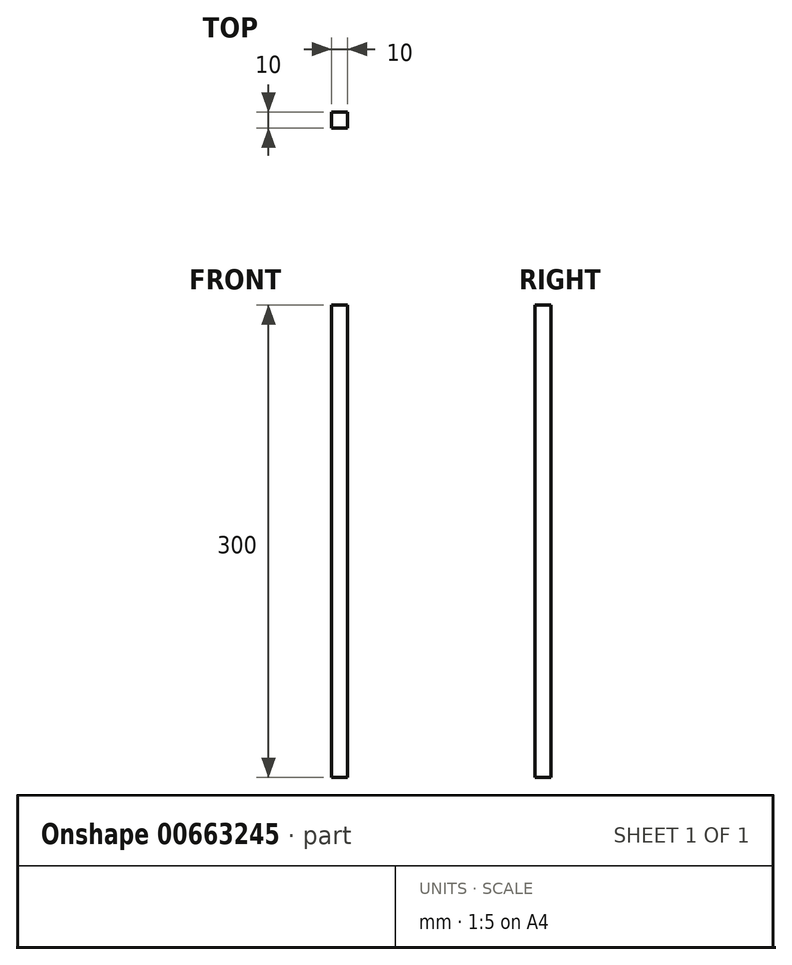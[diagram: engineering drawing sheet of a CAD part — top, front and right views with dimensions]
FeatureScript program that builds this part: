
annotation { "Feature Type Name" : "Feature", "Feature Type Description" : "" }
export const myFeature = defineFeature(function(context is Context, id is Id, definition is map)
    precondition{}
    {
        {
            var Q0;
            Q0=qCreatedBy(makeId("Top.planeOp"),FACE);
            var sketch = newSketch(context, id + "F0", { "sketchPlane" : qUnion([Q0])});
            skLineSegment(sketch, "E0.bottom", {"start": v(5, 5) * mm, "end": v(-5, 5) * mm});
            skLineSegment(sketch, "E0.top", {"start": v(5, -5) * mm, "end": v(-5, -5) * mm});
            skLineSegment(sketch, "E0.left", {"start": v(5, 5) * mm, "end": v(5, -5) * mm});
            skLineSegment(sketch, "E0.right", {"start": v(-5, 5) * mm, "end": v(-5, -5) * mm});
            skPoint(sketch, "E0.middle", {"position": v(0, 0) * mm});
            skSolve(sketch);
        }
        {
            var Q0;
            Q0 = qSketchRegion(id + "F0", true);
            extrude(context, id + "F1", {"entities" : qUnion([Q0]), "depth" : 300 * mm, "offsetDistance" : 25 * mm});
        }
    });
